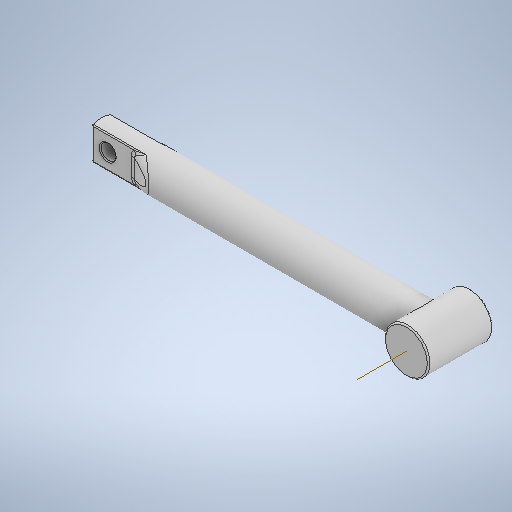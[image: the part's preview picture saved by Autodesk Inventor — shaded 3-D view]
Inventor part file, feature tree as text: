
AUTODESK INVENTOR PART (.ipt)
format: ipt  version: 2025.1 (Build 291241000, 241)  size: 398,848 bytes
history: native  units: mm
features: fillet x4, sketch x4, extrude x3, chamfer x2, revolve x1, other x1
ambient origin geometry x8: Origin, YZ Plane, XZ Plane, XY Plane, X Axis, Y Axis, Z Axis, Center Point
bodies: Volumenkörper1 (feature_tree)
feature tree (15):
  revolve  "Umdrehung1"
  extrude  "Extrusion1"  Depth=4.0mm
  extrude  "Extrusion2"  Depth=35.0mm
  fillet  "Rundung5"  [1 undecoded]
  extrude  "Extrusion3"  Depth=14.0mm TaperAngle=0.0deg
  chamfer  "Fasen1"  Distance=12.0mm
  chamfer  "Fasen2"  Distance=0.3mm
  fillet  "Rundung9"  Radius=14.0mm
  fillet  "Rundung10"  Radius=9.0mm
  fillet  "Rundung11"  [1 undecoded]
  other  "Arbeitsachse1"
  sketch  "Skizze1"  dims[d0=73.5mm d1=4.0mm]
  sketch  "Skizze2"  dims[d2=0.0mm d3=35.0mm d4=90.0deg]
  sketch  "Skizze4"  dims[d5=9.7mm d6=14.0mm d7=0.0mm]
  sketch  "Skizze6"  dims[d15=2.0mm d16=12.0mm d17=5.0mm d18=0.0mm d19=0.0mm d24=0.3mm d31=14.0mm d33=9.0mm d36=0.0mm d39=3.3mm d40=0.0mm d41=70.0mm d42=6.0mm d43=0.0mm d44=0.2mm d45=2.0mm d46=45.0deg d47=0.2mm d48=2.0mm d49=45.0deg d50=2.0mm d51=0.3mm d52=2.0mm d20=0.0mm d21=0.0mm d22=0.0mm d23=0.0mm]
note: 2 required parameter values undecoded (feature->parameter linkage not recoverable at this tier; creation-order binding heuristic only, values carry confidence <= 0.55)
